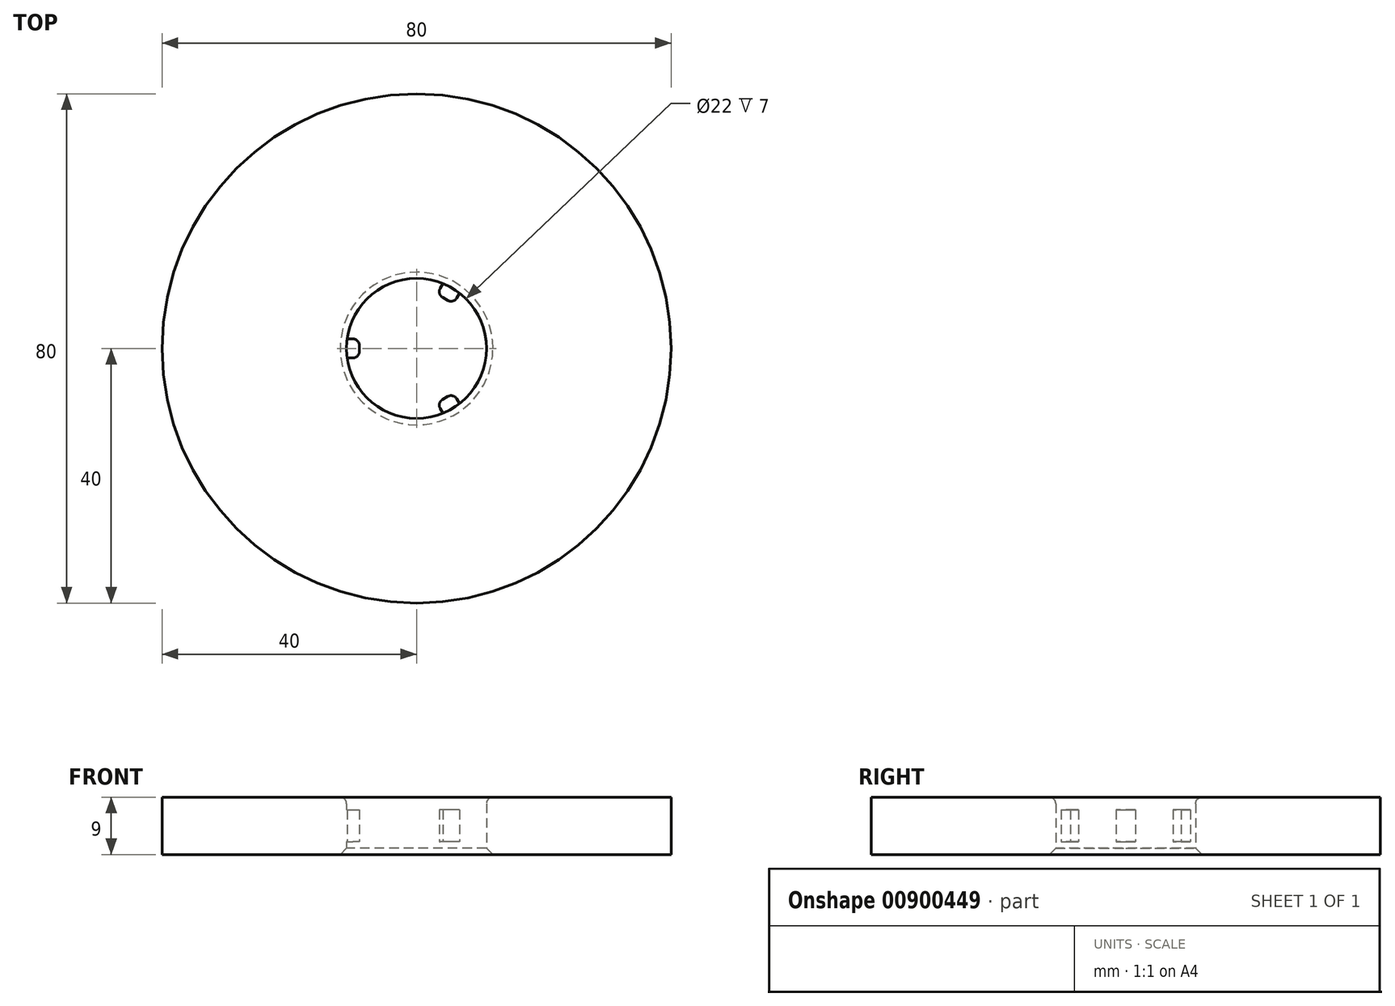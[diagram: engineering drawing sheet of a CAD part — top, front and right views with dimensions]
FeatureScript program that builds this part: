
annotation { "Feature Type Name" : "Feature", "Feature Type Description" : "" }
export const myFeature = defineFeature(function(context is Context, id is Id, definition is map)
    precondition{}
    {
        {
            var Q0;
            Q0=qCreatedBy(makeId("Top.planeOp"),FACE);
            var sketch = newSketch(context, id + "F0", { "sketchPlane" : qUnion([Q0])});
            skCircle(sketch, "E0", {"center": v(0, 0) * mm, "radius": 11 * mm});
            skCircle(sketch, "E1", {"center": v(0, 0) * mm, "radius": 40 * mm});
            skSolve(sketch);
        }
        {
            var Q0;
            Q0=makeQuery(id+"F0.imprint","IMPRINT",FACE,{"disambiguationData":[TD([[makeQuery(id+"F0.imprint","IMPRINT",EDGE,{"derivedFrom":sQuery(id+"F0.wireOp",EDGE,"E0")}),-1.0]])]});
            extrude(context, id + "F1", {"entities" : qUnion([Q0]), "depth" : 9 * mm, "offsetDistance" : 25 * mm});
        }
        {
            var Q0;
            Q0=makeQuery(id+"F1.opExtrude","CAP_EDGE",EDGE,{"disambiguationData":[OSD([sQuery(id+"F0.wireOp",EDGE,"E0")])],"isStart":false});
            fillet(context, id + "F2", {"entities" : qUnion([Q0]), "radius" : 1 * mm, "tangentPropagation" : true, "allowEdgeOverflow" : false});
        }
        {
            var Q0;
            Q0=makeQuery(id+"F1.opExtrude","CAP_EDGE",EDGE,{"disambiguationData":[OSD([sQuery(id+"F0.wireOp",EDGE,"E0")])],"isStart":true});
            chamfer(context, id + "F3", {"entities" : qUnion([Q0]), "width" : 1 * mm, "tangentPropagation" : true});
        }
        {
            var Q0;
            Q0=makeQuery(id+"F1.opExtrude","CAP_FACE",FACE,{"disambiguationData":[OSD([sQuery(id+"F0.wireOp",EDGE,"E0"),sQuery(id+"F0.wireOp",EDGE,"E1")])],"isStart":false});
            var sketch = newSketch(context, id + "F4", { "sketchPlane" : qUnion([Q0])});
            skCircle(sketch, "E2.0", {"center": v(0, 0) * mm, "radius": 11 * mm});
            skLineSegment(sketch, "E3", {"start": v(-11, 0) * mm, "end": v(11, 0) * mm, "construction": true});
            skSolve(sketch);
        }
        {
            var Q0;
            Q0=sQuery(id+"F4.wireOp",EDGE,"E3");
            cPlane(context, id + "F5", {"entities" : qUnion([Q0]), "cplaneType" : CPlaneType.LINE_ANGLE, "offset" : 25 * mm, "angle" : 0 * degree, "width" : 150 * mm, "height" : 150 * mm});
        }
        {
            var Q0;
            Q0=qCreatedBy(id+"F5.planeOp",FACE);
            var sketch = newSketch(context, id + "F6", { "sketchPlane" : qUnion([Q0])});
            skLineSegment(sketch, "E4", {"start": v(14.85, 1) * mm, "end": v(-13.79, 1) * mm, "construction": true});
            skLineSegment(sketch, "E5", {"start": v(17.03, 8) * mm, "end": v(-21.33, 8) * mm, "construction": true});
            skLineSegment(sketch, "E6", {"start": v(0, 1) * mm, "end": v(0, 8) * mm, "construction": true});
            skPoint(sketch, "E7", {"position": v(0, 4.5) * mm});
            skLineSegment(sketch, "E8", {"start": v(10.47, 4.5) * mm, "end": v(-13.39, 4.5) * mm, "construction": true});
            skSolve(sketch);
        }
        {
            var Q0;
            Q0=sQuery(id+"F6.wireOp",EDGE,"E8");
            cPlane(context, id + "F7", {"entities" : qUnion([Q0]), "cplaneType" : CPlaneType.LINE_ANGLE, "offset" : 25 * mm, "angle" : 90 * degree, "width" : 150 * mm, "height" : 150 * mm});
        }
        {
            var Q0;
            Q0=qCreatedBy(id+"F7.planeOp",FACE);
            var sketch = newSketch(context, id + "F8", { "sketchPlane" : qUnion([Q0])});
            skCircle(sketch, "E9.0", {"center": v(0, 0) * mm, "radius": 11 * mm, "construction": true});
            skLineSegment(sketch, "E10.bottom", {"start": v(-12, -1.5) * mm, "end": v(-10, -1.5) * mm});
            skLineSegment(sketch, "E10.top", {"start": v(-12, 1.5) * mm, "end": v(-10, 1.5) * mm});
            skLineSegment(sketch, "E10.left", {"start": v(-12, -1.5) * mm, "end": v(-12, 1.5) * mm});
            skLineSegment(sketch, "E10.right", {"start": v(-9, -0.5) * mm, "end": v(-9, 0.5) * mm});
            skPoint(sketch, "E11", {"position": v(-9, 0) * mm});
            skPoint(sketch, "E12.visualSharp", {"position": v(-9, -1.5) * mm});
            skArc(sketch, "E12.filletArc", {"start": v(-10, -1.5) * mm, "mid": v(-9.3, -1.2) * mm, "end": v(-9, -0.5) * mm});
            skPoint(sketch, "E13.visualSharp", {"position": v(-9, 1.5) * mm});
            skArc(sketch, "E13.filletArc", {"start": v(-9, 0.5) * mm, "mid": v(-9.3, 1.2) * mm, "end": v(-10, 1.5) * mm});
            skLineSegment(sketch, "E14.1.0", {"start": v(7.3, -9.64) * mm, "end": v(4.7, -11.14) * mm});
            skPoint(sketch, "E14.1.1", {"position": v(3.2, -8.54) * mm});
            skLineSegment(sketch, "E14.1.2", {"start": v(4.7, -11.14) * mm, "end": v(3.7, -9.41) * mm});
            skLineSegment(sketch, "E14.1.3", {"start": v(7.3, -9.64) * mm, "end": v(6.3, -7.91) * mm});
            skPoint(sketch, "E14.1.4", {"position": v(5.8, -7.04) * mm});
            skPoint(sketch, "E14.1.5", {"position": v(4.5, -7.8) * mm});
            skArc(sketch, "E14.1.6", {"start": v(6.3, -7.91) * mm, "mid": v(5.7, -7.44) * mm, "end": v(4.93, -7.54) * mm});
            skArc(sketch, "E14.1.7", {"start": v(4.07, -8.04) * mm, "mid": v(3.6, -8.65) * mm, "end": v(3.7, -9.41) * mm});
            skLineSegment(sketch, "E14.1.8", {"start": v(4.93, -7.54) * mm, "end": v(4.07, -8.04) * mm});
            skLineSegment(sketch, "E14.2.0", {"start": v(4.7, 11.14) * mm, "end": v(7.3, 9.64) * mm});
            skPoint(sketch, "E14.2.1", {"position": v(5.8, 7.04) * mm});
            skLineSegment(sketch, "E14.2.2", {"start": v(7.3, 9.64) * mm, "end": v(6.3, 7.91) * mm});
            skLineSegment(sketch, "E14.2.3", {"start": v(4.7, 11.14) * mm, "end": v(3.7, 9.41) * mm});
            skPoint(sketch, "E14.2.4", {"position": v(3.2, 8.54) * mm});
            skPoint(sketch, "E14.2.5", {"position": v(4.5, 7.8) * mm});
            skArc(sketch, "E14.2.6", {"start": v(3.7, 9.41) * mm, "mid": v(3.6, 8.65) * mm, "end": v(4.07, 8.04) * mm});
            skArc(sketch, "E14.2.7", {"start": v(4.93, 7.54) * mm, "mid": v(5.7, 7.44) * mm, "end": v(6.3, 7.91) * mm});
            skLineSegment(sketch, "E14.2.8", {"start": v(4.07, 8.04) * mm, "end": v(4.93, 7.54) * mm});
            skSolve(sketch);
        }
        {
            var Q0;
            Q0 = qSketchRegion(id + "F8", true);
            extrude(context, id + "F9", {"entities" : qUnion([Q0]), "operationType" : NewBodyOperationType.ADD, "endBound" : BoundingType.SYMMETRIC, "depth" : 5 * mm, "offsetDistance" : 25 * mm});
        }
    });
